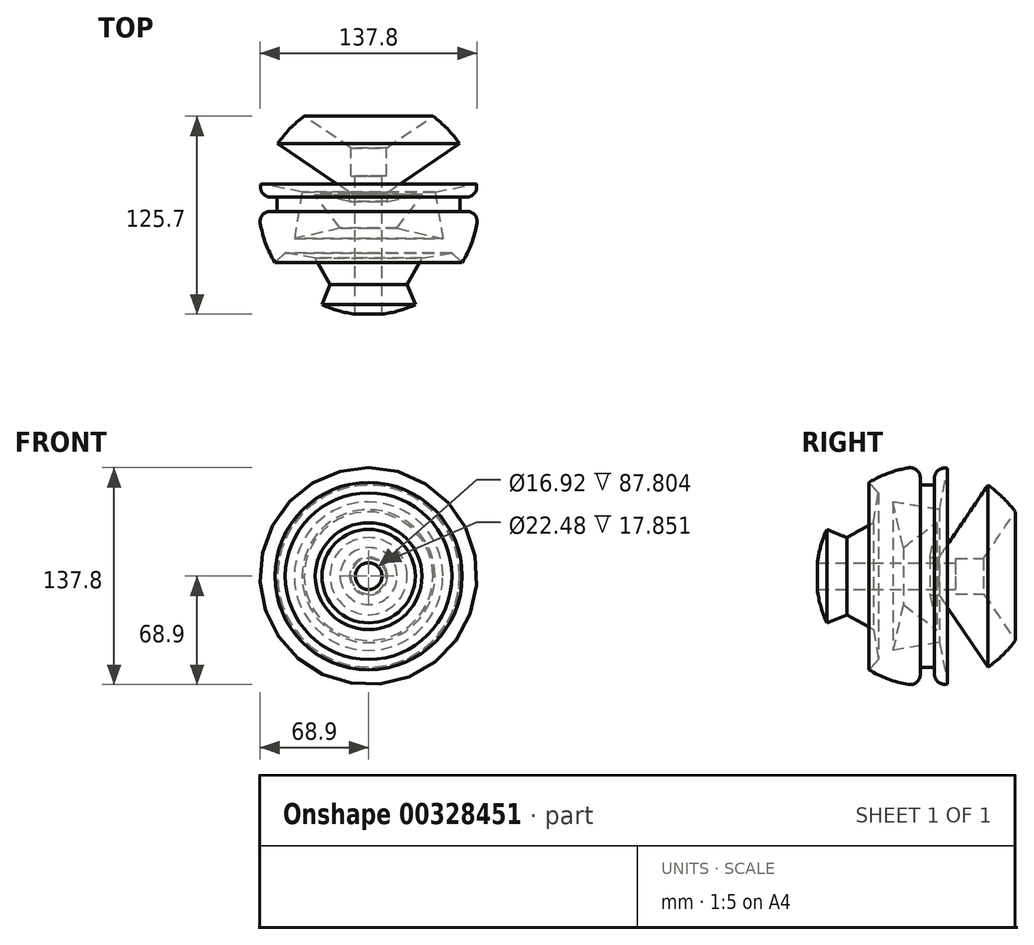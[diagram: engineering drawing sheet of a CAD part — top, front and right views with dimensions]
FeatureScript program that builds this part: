
annotation { "Feature Type Name" : "Feature", "Feature Type Description" : "" }
export const myFeature = defineFeature(function(context is Context, id is Id, definition is map)
    precondition{}
    {
        {
            var Q0;
            Q0=qCreatedBy(makeId("Top.planeOp"),FACE);
            var sketch = newSketch(context, id + "F0", { "sketchPlane" : qUnion([Q0])});
            skArc(sketch, "E0", {"start": v(-68.81, -11.25) * mm, "mid": v(-65.36, -24.28) * mm, "end": v(-59.47, -36.4) * mm});
            skLineSegment(sketch, "E1", {"start": v(-62.32, 5.18) * mm, "end": v(-58.07, 5.18) * mm});
            skLineSegment(sketch, "E2", {"start": v(-58.07, 5.18) * mm, "end": v(-58.07, -3.87) * mm});
            skLineSegment(sketch, "E3", {"start": v(-58.07, -3.87) * mm, "end": v(-62.55, -3.87) * mm});
            skLineSegment(sketch, "E4", {"start": v(0, 69.72) * mm, "end": v(0, -69.72) * mm});
            skLineSegment(sketch, "E5", {"start": v(-57.75, 39.07) * mm, "end": v(-12, 8.13) * mm});
            skLineSegment(sketch, "E6", {"start": v(-12, 2.38) * mm, "end": v(-34.2, 6.78) * mm});
            skLineSegment(sketch, "E7", {"start": v(-40.87, 56.5) * mm, "end": v(-11.24, 36.45) * mm});
            skLineSegment(sketch, "E8", {"start": v(0, 28.84) * mm, "end": v(0, 69.72) * mm});
            skArc(sketch, "E9.trimOffspring", {"start": v(-40.87, 56.5) * mm, "mid": v(-50.07, 48.52) * mm, "end": v(-57.75, 39.07) * mm});
            skArc(sketch, "E10.trimOffspring", {"start": v(-68.4, 13.55) * mm, "mid": v(-68.48, 13.12) * mm, "end": v(-68.56, 12.69) * mm});
            skPoint(sketch, "E11.visualSharp", {"position": v(-69.62, -3.87) * mm});
            skArc(sketch, "E11.filletArc", {"start": v(-62.55, -3.87) * mm, "mid": v(-67.38, -6.1) * mm, "end": v(-68.81, -11.25) * mm});
            skPoint(sketch, "E12.visualSharp", {"position": v(-69.53, 5.18) * mm});
            skArc(sketch, "E12.filletArc", {"start": v(-68.56, 12.69) * mm, "mid": v(-67.2, 7.47) * mm, "end": v(-62.32, 5.18) * mm});
            skArc(sketch, "E13.cCircle", {"start": v(-30.04, -62.92) * mm, "mid": v(-33.58, -36.66) * mm, "end": v(-60.07, -36.92) * mm, "construction": true});
            skLineSegment(sketch, "E13.0", {"start": v(-33.89, -33.63) * mm, "end": v(-24.5, -50.47) * mm});
            skLineSegment(sketch, "E13.1", {"start": v(-24.5, -50.47) * mm, "end": v(-29.68, -63.1) * mm});
            skLineSegment(sketch, "E13.5", {"start": v(-60.07, -36.92) * mm, "end": v(-52.9, -30.47) * mm});
            skLineSegment(sketch, "E13.6", {"start": v(-52.9, -30.47) * mm, "end": v(-33.89, -33.63) * mm});
            skPoint(sketch, "E13.0.midPoint", {"position": v(-29.2, -42.05) * mm});
            skArc(sketch, "E14.trimOffspring", {"start": v(-30.04, -62.92) * mm, "mid": v(-19.5, -66.94) * mm, "end": v(-8.46, -69.2) * mm});
            skPoint(sketch, "E15.orphan", {"position": v(-67.23, -43.37) * mm});
            skLineSegment(sketch, "E16", {"start": v(-42.25, 8.37) * mm, "end": v(-47.17, -21.23) * mm});
            skPoint(sketch, "E16.endSnap0", {"position": v(-43.4, -32.05) * mm});
            skLineSegment(sketch, "E17", {"start": v(-34.2, 6.78) * mm, "end": v(-18.12, -14.61) * mm});
            skLineSegment(sketch, "E18", {"start": v(-18.12, -14.61) * mm, "end": v(-47.17, -21.23) * mm});
            skLineSegment(sketch, "E19.trimOffspring", {"start": v(-48.82, -31.15) * mm, "end": v(-48.97, -32.05) * mm});
            skLineSegment(sketch, "E20.trimOffspring", {"start": v(-42.25, 8.37) * mm, "end": v(-68.4, 13.55) * mm});
            skLineSegment(sketch, "E21", {"start": v(-8.46, 18.6) * mm, "end": v(-8.46, -69.2) * mm});
            skLineSegment(sketch, "E22", {"start": v(-11.24, 36.45) * mm, "end": v(-11.24, 18.6) * mm});
            skLineSegment(sketch, "E23", {"start": v(-11.24, 18.6) * mm, "end": v(-8.46, 18.6) * mm});
            skPoint(sketch, "E24.orphan", {"position": v(-8.46, 34.57) * mm});
            skLineSegment(sketch, "E25", {"start": v(-12, 2.38) * mm, "end": v(-12, 8.13) * mm});
            skSolve(sketch);
        }
        {
            var Q0;
            {var subQ0=sQuery(id+"F0.wireOp",EDGE,"E1");Q0=makeQuery(id+"F0.imprint","IMPRINT",FACE,{"disambiguationData":[TD([[makeQuery(id+"F0.imprint","IMPRINT",EDGE,{"derivedFrom":subQ0}),1.0]])]});}
            var Q1;
            {var subQ2=sQuery(id+"F0.wireOp",EDGE,"E5");Q1=makeQuery(id+"F0.imprint","IMPRINT",FACE,{"disambiguationData":[TD([[makeQuery(id+"F0.imprint","IMPRINT",EDGE,{"derivedFrom":subQ2}),1.0]])]});}
            var Q2;
            Q2=sQuery(id+"F0.wireOp",EDGE,"E4");
            revolve(context, id + "F1", {"entities" : qUnion([Q0, Q1]), "axis" : qUnion([Q2]), "revolveType" : RevolveType.FULL});
        }
    });
